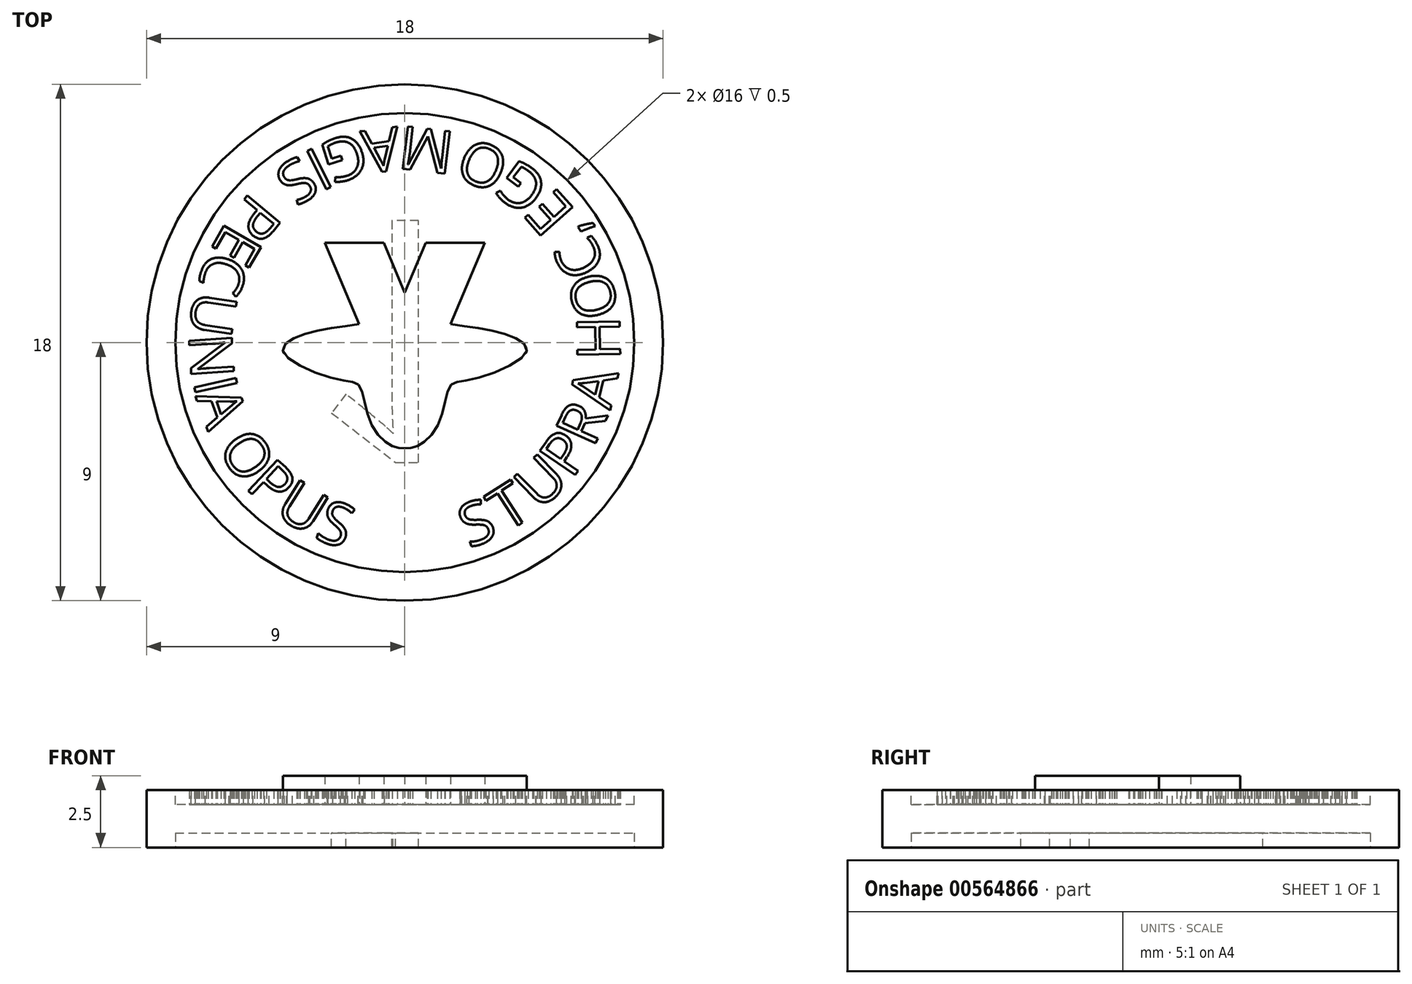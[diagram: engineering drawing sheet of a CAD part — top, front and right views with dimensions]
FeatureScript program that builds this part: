
annotation { "Feature Type Name" : "Feature", "Feature Type Description" : "" }
export const myFeature = defineFeature(function(context is Context, id is Id, definition is map)
    precondition{}
    {
        {
            assignVariable(context, id + "F0", {"name" : "ImpressionDepth", "anyValue" : 0.5});
        }
        {
            assignVariable(context, id + "F1", {"name" : "EmbossHeight", "anyValue" : 0.5});
        }
        {
            var Q0;
            Q0=qCreatedBy(makeId("Top.planeOp"),FACE);
            var sketch = newSketch(context, id + "F2", { "sketchPlane" : qUnion([Q0])});
            skCircle(sketch, "E0", {"center": v(0, 0) * mm, "radius": 9 * mm});
            skSolve(sketch);
        }
        {
            var Q0;
            Q0=qSketchRegion(id+"F2",true);
            extrude(context, id + "F3", {"entities" : qUnion([Q0]), "depth" : 2 * mm});
        }
        {
            var Q0;
            Q0=makeQuery(id+"F3.opExtrude","CAP_FACE",FACE,{"disambiguationData":[OSD([sQuery(id+"F2.wireOp",EDGE,"E0")])],"isStart":false});
            var sketch = newSketch(context, id + "F4", { "sketchPlane" : qUnion([Q0])});
            skCircle(sketch, "E1.0", {"center": v(0, 0) * mm, "radius": 8 * mm});
            skSolve(sketch);
        }
        {
            var Q0;
            Q0=qSketchRegion(id+"F4",true);
            extrude(context, id + "F5", {"entities" : qUnion([Q0]), "operationType" : NewBodyOperationType.REMOVE, "oppositeDirection" : true, "depth" : (getVariable(context, 'ImpressionDepth')) * mm});
        }
        {
            var Q0;
            Q0=makeQuery(id+"F3.opExtrude","CAP_FACE",FACE,{"disambiguationData":[OSD([sQuery(id+"F2.wireOp",EDGE,"E0")])],"isStart":true});
            var sketch = newSketch(context, id + "F6", { "sketchPlane" : qUnion([Q0])});
            skCircle(sketch, "E2.0", {"center": v(0, 0) * mm, "radius": 8 * mm});
            skSolve(sketch);
        }
        {
            var Q0;
            Q0=qSketchRegion(id+"F6",true);
            extrude(context, id + "F7", {"entities" : qUnion([Q0]), "operationType" : NewBodyOperationType.REMOVE, "oppositeDirection" : true, "depth" : (getVariable(context, 'ImpressionDepth')) * mm});
        }
        {
            var Q0;
            Q0=makeQuery(id+"F7.boolean.opBoolean","COPY",FACE,{"derivedFrom":makeQuery(id+"F7.opExtrude","CAP_FACE",FACE,{"disambiguationData":[OSD([sQuery(id+"F6.wireOp",EDGE,"E2.0")])],"isStart":false})});
            var sketch = newSketch(context, id + "F8", { "sketchPlane" : qUnion([Q0])});
            skText(sketch, "E3", { "text": "1", "fontName": "OpenSans-Regular.ttf"});
            skPoint(sketch, "E4", {"position": v(-1.2, 0) * mm});
            skLineSegment(sketch, "E5", {"start": v(-1.2, 0) * mm, "end": v(0, 0) * mm, "construction": true});
            const initialGuessF8  = {"E3": [-0.00364, -0.00425, 1, 0, 0.0085]};
            skSetInitialGuess(sketch, initialGuessF8);
            skSolve(sketch);
        }
        {
            var Q0;
            Q0=qSketchRegion(id+"F8",true);
            extrude(context, id + "F9", {"entities" : qUnion([Q0]), "operationType" : NewBodyOperationType.ADD, "depth" : (getVariable(context, 'EmbossHeight')) * mm});
        }
        {
            var Q0;
            Q0=makeQuery(id+"F5.boolean.opBoolean","COPY",FACE,{"derivedFrom":makeQuery(id+"F5.opExtrude","CAP_FACE",FACE,{"disambiguationData":[OSD([sQuery(id+"F4.wireOp",EDGE,"E1.0")])],"isStart":false})});
            var sketch = newSketch(context, id + "F10", { "sketchPlane" : qUnion([Q0])});
            skLineSegment(sketch, "E6", {"start": v(0, -8) * mm, "end": v(0, 8) * mm, "construction": true});
            skLineSegment(sketch, "E7", {"start": v(0, 1.74) * mm, "end": v(-0.74, 3.47) * mm});
            skLineSegment(sketch, "E8", {"start": v(-0.74, 3.47) * mm, "end": v(-2.79, 3.47) * mm});
            skLineSegment(sketch, "E9", {"start": v(-2.79, 3.47) * mm, "end": v(-1.59, 0.64) * mm});
            skLineSegment(sketch, "E10.MirrorCS", {"start": v(0, 1.74) * mm, "end": v(0.74, 3.47) * mm});
            skLineSegment(sketch, "E11.MirrorCS", {"start": v(2.79, 3.47) * mm, "end": v(1.59, 0.64) * mm});
            skLineSegment(sketch, "E12.MirrorCS", {"start": v(0.74, 3.47) * mm, "end": v(2.79, 3.47) * mm});
            skFitSpline(sketch, "E13", {"points": [v(-1.59, 0.64) * mm, v(-3.63, 0.25) * mm, v(-4.24, -0.32) * mm, v(-2.25, -1.3) * mm, v(-1.59, -1.5) * mm, v(-1.19, -2.8) * mm, v(-0.45, -3.6) * mm, v(0, -3.68) * mm], "startDerivative": vector(-11.02, -1.68) * mm, "endDerivative": vector(4.81, 0) * mm});
            skFitSpline(sketch, "E14.MirrorCS", {"points": [v(1.59, 0.64) * mm, v(3.63, 0.25) * mm, v(4.24, -0.32) * mm, v(2.25, -1.3) * mm, v(1.59, -1.5) * mm, v(1.19, -2.8) * mm, v(0.45, -3.6) * mm, v(0, -3.68) * mm], "startDerivative": vector(11.02, -1.68) * mm, "endDerivative": vector(-4.81, 0) * mm});
            skSolve(sketch);
        }
        {
            var Q0;
            Q0=qSketchRegion(id+"F10",true);
            extrude(context, id + "F11", {"entities" : qUnion([Q0]), "operationType" : NewBodyOperationType.ADD, "depth" : 1 * mm});
        }
        {
            var Q0;
            Q0=makeQuery(id+"F5.boolean.opBoolean","COPY",FACE,{"derivedFrom":makeQuery(id+"F5.opExtrude","CAP_FACE",FACE,{"disambiguationData":[OSD([sQuery(id+"F4.wireOp",EDGE,"E1.0")])],"isStart":false})});
            var sketch = newSketch(context, id + "F12", { "sketchPlane" : qUnion([Q0])});
            skCircle(sketch, "E15.0", {"center": v(0, 0) * mm, "radius": 7.5 * mm, "construction": true});
            skText(sketch, "E16", { "text": "S", "fontName": "OpenSans-Regular.ttf"});
            skText(sketch, "E17", { "text": "I", "fontName": "OpenSans-Regular.ttf"});
            skText(sketch, "E18", { "text": "G", "fontName": "OpenSans-Regular.ttf"});
            skText(sketch, "E19", { "text": "A", "fontName": "OpenSans-Regular.ttf"});
            skLineSegment(sketch, "E20", {"start": v(0, 0) * mm, "end": v(0, 7.5) * mm, "construction": true});
            skText(sketch, "E21", { "text": "M", "fontName": "OpenSans-Regular.ttf"});
            skText(sketch, "E22", { "text": "P", "fontName": "OpenSans-Regular.ttf"});
            skText(sketch, "E23", { "text": "E", "fontName": "OpenSans-Regular.ttf"});
            skText(sketch, "E24", { "text": "C", "fontName": "OpenSans-Regular.ttf"});
            skText(sketch, "E25", { "text": "U", "fontName": "OpenSans-Regular.ttf"});
            skText(sketch, "E26", { "text": "N", "fontName": "OpenSans-Regular.ttf"});
            skText(sketch, "E27", { "text": "I", "fontName": "OpenSans-Regular.ttf"});
            skText(sketch, "E28", { "text": "A", "fontName": "OpenSans-Regular.ttf"});
            skPoint(sketch, "E29", {"position": v(-6.14, 2.87) * mm});
            skText(sketch, "E30", { "text": "O", "fontName": "OpenSans-Regular.ttf"});
            skText(sketch, "E31", { "text": "P", "fontName": "OpenSans-Regular.ttf"});
            skText(sketch, "E32", { "text": "U", "fontName": "OpenSans-Regular.ttf"});
            skText(sketch, "E33", { "text": "S", "fontName": "OpenSans-Regular.ttf"});
            skText(sketch, "E34", { "text": "S", "fontName": "OpenSans-Regular.ttf"});
            skText(sketch, "E35", { "text": "T", "fontName": "OpenSans-Regular.ttf"});
            skText(sketch, "E36", { "text": "U", "fontName": "OpenSans-Regular.ttf"});
            skText(sketch, "E37", { "text": "P", "fontName": "OpenSans-Regular.ttf"});
            skText(sketch, "E38", { "text": "R", "fontName": "OpenSans-Regular.ttf"});
            skText(sketch, "E39", { "text": "A", "fontName": "OpenSans-Regular.ttf"});
            skText(sketch, "E40", { "text": "H", "fontName": "OpenSans-Regular.ttf"});
            skText(sketch, "E41", { "text": "O", "fontName": "OpenSans-Regular.ttf"});
            skText(sketch, "E42", { "text": "C", "fontName": "OpenSans-Regular.ttf"});
            skText(sketch, "E43", { "text": ",", "fontName": "OpenSans-Regular.ttf"});
            skText(sketch, "E44", { "text": "E", "fontName": "OpenSans-Regular.ttf"});
            skText(sketch, "E45", { "text": "G", "fontName": "OpenSans-Regular.ttf"});
            skText(sketch, "E46", { "text": "O", "fontName": "OpenSans-Regular.ttf"});
            const initialGuessF12  = {"E16": [-0.00369, 0.00656, -0.83068, -0.55674, 0.0015], "E17": [-0.00292, 0.00525, 0.89418, 0.44771, 0.0015], "E18": [-0.0016, 0.00737, -0.9513, -0.30828, 0.0015], "E19": [-0.00026, 0.00753, -0.99144, -0.13053, 0.0015], "E21": [0.00177, 0.00734, -0.9933, 0.1156, 0.0015], "E22": [-0.00536, 0.00528, -0.63874, -0.76943, 0.0015], "E23": [-0.0062, 0.00425, -0.49963, -0.86624, 0.0015], "E24": [-0.00678, 0.00327, -0.34943, -0.93696, 0.0015], "E25": [-0.00731, 0.00183, -0.14699, -0.98914, 0.0015], "E26": [-0.00753, 0.00027, 0.06408, -0.99794, 0.0015], "E27": [-0.00738, -0.00136, 0.21531, -0.97655, 0.0015], "E28": [-0.0073, -0.00187, 0.34016, -0.94037, 0.0015], "E30": [-0.00657, -0.0037, 0.58166, -0.81343, 0.0015], "E31": [-0.0056, -0.00503, 0.72875, -0.68478, 0.0015], "E32": [-0.0046, -0.00596, 0.84697, -0.53165, 0.0015], "E33": [-0.00319, -0.00681, 0.93625, -0.35134, 0.0015], "E34": [0.00224, -0.00718, 0.9286, 0.37107, 0.0015], "E35": [0.00354, -0.00664, 0.83977, 0.54294, 0.0015], "E36": [0.0047, -0.00589, 0.7171, 0.69698, 0.0015], "E37": [0.00582, -0.00478, 0.56662, 0.82398, 0.0015], "E38": [0.00657, -0.00369, 0.407, 0.91343, 0.0015], "E39": [0.00716, -0.00236, 0.22024, 0.97545, 0.0015], "E40": [0.00751, -0.0006, -0.0188, 0.99982, 0.0015], "E41": [0.00748, 0.00102, -0.24105, 0.97051, 0.0015], "E42": [0.00705, 0.00266, -0.43832, 0.89882, 0.0015], "E43": [0.00644, 0.00386, -0.54254, 0.84003, 0.0015], "E44": [0.00598, 0.00457, -0.66727, 0.74481, 0.0015], "E45": [0.00511, 0.00554, -0.7985, 0.602, 0.0015], "E46": [0.00375, 0.00654, -0.9161, 0.40096, 0.0015]};
            skSetInitialGuess(sketch, initialGuessF12);
            skSolve(sketch);
        }
        {
            var Q0;
            Q0=qSketchRegion(id+"F12",true);
            extrude(context, id + "F13", {"entities" : qUnion([Q0]), "operationType" : NewBodyOperationType.ADD, "depth" : (getVariable(context, 'EmbossHeight')) * mm});
        }
    });
